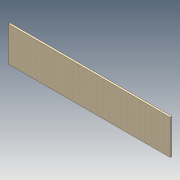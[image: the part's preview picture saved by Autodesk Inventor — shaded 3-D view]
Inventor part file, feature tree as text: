
AUTODESK INVENTOR PART (.ipt)
format: ipt  version: 2012 (Build 160160000, 160)  size: 72,192 bytes
history: native  units: in
note: dims shown in document units (in); Inventor stores cm internally (conversion verified against a paired STEP export)
features: extrude x1, sketch x1
ambient origin geometry x8: Origin, YZ Plane, XZ Plane, XY Plane, X Axis, Y Axis, Z Axis, Center Point
bodies: Solid1 (feature_tree)
feature tree (2):
  extrude  "Extrusion1"  Depth=44.25in
  sketch  "Sketch1"  dims[d0=9.5in d1=44.25in d2=0.5in d3=0.0in]
